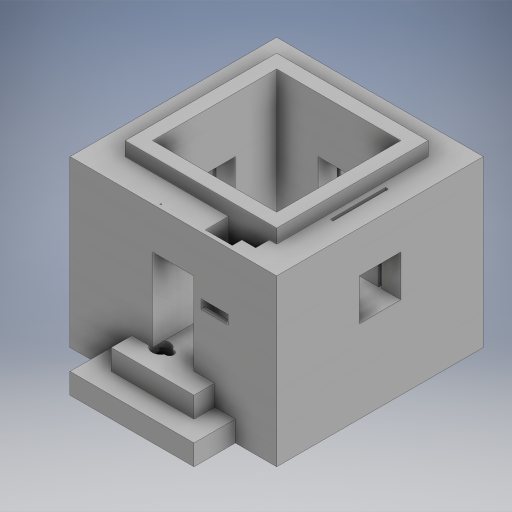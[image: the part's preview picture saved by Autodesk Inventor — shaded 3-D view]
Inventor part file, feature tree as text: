
AUTODESK INVENTOR PART (.ipt)
format: ipt  version: 2023 (Build 270158000, 158)  size: 485,888 bytes
history: native  units: mm
features: sketch x17, extrude x16, other x1, hole x1
ambient origin geometry x8: Origin, YZ Plane, XZ Plane, XY Plane, X Axis, Y Axis, Z Axis, Center Point
bodies: Body1 (feature_tree)
feature tree (35):
  other  "Těleso1"
  extrude  "Vysunutí1"  Depth=150.0mm
  extrude  "Vysunutí2"  Depth=150.0mm
  extrude  "Vysunutí3"  Depth=30.0mm TaperAngle=0.0deg
  extrude  "Vysunutí4"  Depth=150.0mm
  extrude  "Vysunutí5"  Depth=150.0mm
  extrude  "Vysunutí6"  Depth=90.0mm
  extrude  "Vysunutí7"  Depth=90.0mm
  hole  "Díra1"  [1 undecoded]
  extrude  "Vysunutí9"  Depth=30.0mm
  extrude  "Vysunutí10"  Depth=60.0mm
  extrude  "Vysunutí12"  Depth=90.0mm TaperAngle=0.0deg
  extrude  "Vysunutí14"  Depth=30.0mm
  extrude  "Vysunutí15"  Depth=30.0mm
  extrude  "Vysunutí16"  Depth=30.0mm TaperAngle=0.0deg
  extrude  "Vysunutí17"  Depth=30.0mm
  extrude  "Vysunutí18"  Depth=30.0mm
  extrude  "Vysunutí19"  TaperAngle=0.0deg  [1 undecoded]
  sketch  "Náčrt1"
  sketch  "Náčrt2"
  sketch  "Náčrt3"
  sketch  "Náčrt4"
  sketch  "Náčrt5"
  sketch  "Náčrt6"
  sketch  "Náčrt7"
  sketch  "Náčrt9"
  sketch  "Náčrt10"
  sketch  "Náčrt11"
  sketch  "Náčrt13"
  sketch  "Náčrt15"
  sketch  "Náčrt16"
  sketch  "Náčrt17"
  sketch  "Náčrt18"
  sketch  "Náčrt19"
  sketch  "Náčrt20"
note: 2 required parameter values undecoded (feature->parameter linkage not recoverable at this tier; creation-order binding heuristic only, values carry confidence <= 0.55)
